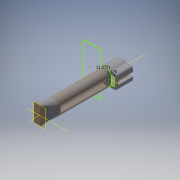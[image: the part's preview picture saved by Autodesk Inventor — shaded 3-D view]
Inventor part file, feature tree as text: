
AUTODESK INVENTOR PART (.ipt)
format: ipt  version: 2016 (Build 200138000, 138)  size: 378,880 bytes
history: native  units: mm
features: other x8, extrude x7, sketch x6, thicken_offset x3, fillet x3, hole x2, plane x2, boolean_combine x1, draft x1, loft x1
ambient origin geometry x8: Origin, YZ Plane, XZ Plane, XY Plane, X Axis, Y Axis, Z Axis, Center Point
bodies: Solid1 (feature_tree), Solid2 (feature_tree), Solid3 (feature_tree)
feature tree (34):
  other  "zero_sketch.ipt"
  other  "2-reel_holder.ipt"
  sketch  "Sketch5"  dims[d1=3.0mm d2=1.5mm d3=1.05mm d4=3.0mm d5=1.05mm d6=2.0mm d9=4.0mm d10=3.0mm]
  thicken_offset  "Thicken1"
  thicken_offset  "Thicken2"
  extrude  "Extrusion1"  Depth=3.0mm
  sketch  "Sketch12"  dims[d16=1.575mm d17=6.0mm d18=0.0mm]
  extrude  "Extrusion3"  Depth=1.575mm
  thicken_offset  "Thicken3"
  extrude  "Extrusion4"  Depth=6.0mm TaperAngle=0.0deg
  hole  "Hole3"  [1 undecoded]
  boolean_combine  "Combine1"
  fillet  "Fillet2"  Radius=1.0mm
  fillet  "Fillet3"  Radius=3.0mm
  draft  "FaceDraft1"
  fillet  "Fillet4"  Radius=5.5mm
  hole  "Hole4"  [1 undecoded]
  plane  "Work Plane2"
  sketch  "Sketch19"  dims[d27=1.5mm d28=0.75mm d29=6.0mm d30=0.0mm d41=0.5mm d42=0.0mm d43=20.0mm d44=0.0mm d45=1.0mm d46=1.0mm d47=1.0mm d49=2.6mm d50=1.3mm d51=20.0mm d52=0.0mm d68=2.25mm d69=6.0mm d70=4.0mm d71=2.0mm d72=90.0deg d73=8.0mm d74=20.594885mm d78=2.0mm d79=1.0mm d80=0.436332mm d81=0.75mm d82=2.05mm d83=6.0mm d84=4.0mm d85=2.0mm d86=90.0deg d87=8.0mm d88=20.594885mm d89=7.0mm d90=10.0mm d8=3.4925mm d92=1.5875mm d93=6.985mm d94=3.4925mm d95=0.0mm d96=90.0deg d97=0.0mm d98=90.0deg d103=10.0mm d104=0.0mm]
  plane  "Work Plane3"
  other  "Work Axis2"
  loft  "Loft2"
  extrude  "Extrusion5"  Depth=10.0mm TaperAngle=0.0deg
  other  "base+body"
  other  "Srf2"
  other  "Srf3"
  sketch  "Sketch8"  dims[d11=1.5mm d15=1.575mm]
  other  "Srf4"
  sketch  "Sketch14"  dims[d19=6.0mm d20=0.0mm d21=1.0mm d22=0.5mm d23=1.0mm d24=0.5mm d25=3.0mm d26=5.5mm]
  sketch  "Sketch1"  dims[d0=10.0mm]
  other  "Edges2"
  extrude  "ExtrusionSrf2"  Depth=10.0mm TaperAngle=0.0deg
  extrude  "ExtrusionSrf3"  Depth=10.0mm
  extrude  "ExtrusionSrf4"  Depth=10.0mm
note: 2 required parameter values undecoded (feature->parameter linkage not recoverable at this tier; creation-order binding heuristic only, values carry confidence <= 0.55)
